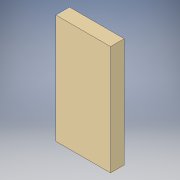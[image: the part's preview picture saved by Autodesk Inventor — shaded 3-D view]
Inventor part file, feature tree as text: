
AUTODESK INVENTOR PART (.ipt)
format: ipt  version: 2019 (Build 230136000, 136)  size: 93,696 bytes
history: native  units: in
note: dims shown in document units (in); Inventor stores cm internally (conversion verified against a paired STEP export)
features: extrude x1, sketch x1
ambient origin geometry x8: Origin, YZ Plane, XZ Plane, XY Plane, X Axis, Y Axis, Z Axis, Center Point
bodies: Solid1 (feature_tree)
feature tree (2):
  extrude  "Extrusion1"  Depth=1.0in
  sketch  "Sketch1"  dims[d0=0.5in d1=1.0in d2=0.125in d3=0.0in]
